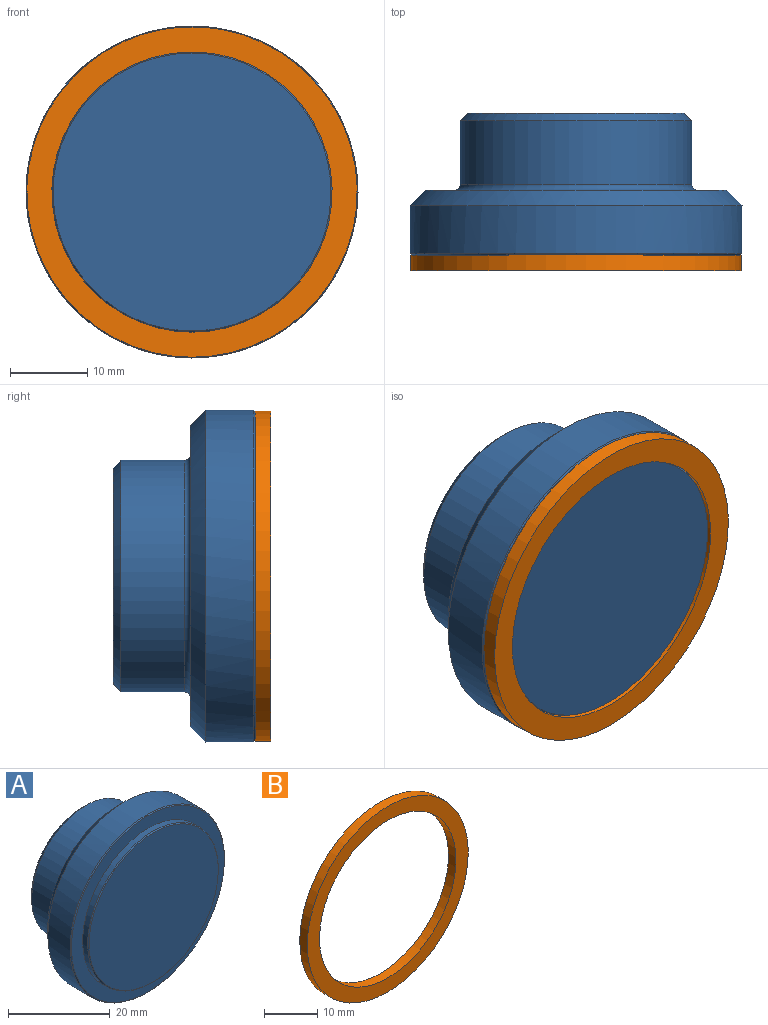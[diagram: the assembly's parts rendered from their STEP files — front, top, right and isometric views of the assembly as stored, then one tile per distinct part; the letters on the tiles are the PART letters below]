
ASSEMBLY  parts=2 mates=1
PART A: 15 faces, bbox 43x20x43 mm
  f0: plane 36x36mm, normal (0,-1,0), area 1017.9mm2, adj f10
  f1: plane 28x28mm, normal (0,1,0), area 565.5mm2, adj f8,f13
  f2: cylinder r=15mm len=30mm, axis (0,1,0), area 772.8mm2, adj f7,f8
  f3: plane 39x39mm, normal (0,1,0), area 410.3mm2, adj f7,f14
  f4: cylinder r=21.5mm len=43mm, axis (0,1,0), area 837.5mm2, adj f9,f14
  f5: plane 42.6x42.6mm, normal (0,-1,0), area 384.7mm2, adj f6,f9
  f6: cylinder r=18.2mm len=36.4mm, axis (0,1,0), area 160.1mm2, adj f5,f10
  f7: torus R=15.8mm, axis (0,-1,0), area 120.7mm2, adj f2,f3
  f8: cone r=14mm half-angle=45deg, axis (0,-1,0), area 128.8mm2, adj f1,f2
  f9: cone r=21.5mm half-angle=45deg, axis (0,1,0), area 38mm2, adj f4,f5
  f10: cone r=18.2mm half-angle=45deg, axis (0,1,0), area 32.2mm2, adj f0,f6
  f11: cylinder r=3mm len=14mm, axis (0,1,0), area 263.9mm2, adj f12,f13
  f12: plane 6x6mm, normal (0,1,0), area 28.3mm2, adj f11
  f13: cone r=3mm half-angle=45deg, axis (0,1,0), area 31.1mm2, adj f1,f11
  f14: cone r=19.5mm half-angle=45deg, axis (0,-1,0), area 364.3mm2, adj f3,f4
PART B: 4 faces, bbox 42.8x2x42.8 mm
  f0: cylinder r=18.15mm len=36.3mm, axis (0,-1,0), area 228.1mm2, adj f2,f3
  f1: cylinder r=21.4mm len=42.8mm, axis (0,-1,0), area 268.9mm2, adj f2,f3
  f2: plane 42.8x42.8mm, normal (0,1,0), area 403.8mm2, adj f0,f1
  f3: plane 42.8x42.8mm, normal (0,-1,0), area 403.8mm2, adj f0,f1
PLACE A t=(6.23,-0.45,8.94)mm
PLACE B t=(6.23,-0.85,8.94)mm
MATE planar B.f1 <-> A.f2  axis (0,1,0) through (6.23,1.15,8.94)mm
